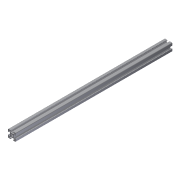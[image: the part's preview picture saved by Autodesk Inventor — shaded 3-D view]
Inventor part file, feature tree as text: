
AUTODESK INVENTOR PART (.ipt)
format: ipt  version: 2011 (Build 150239000, 239)  size: 166,912 bytes
history: native  units: in
note: dims shown in document units (in); Inventor stores cm internally (conversion verified against a paired STEP export)
features: extrude x1, sketch x1
ambient origin geometry x8: Origin, YZ Plane, XZ Plane, XY Plane, X Axis, Y Axis, Z Axis, Center Point
bodies: Solid1 (feature_tree)
feature tree (2):
  extrude  "Extrusion1"  [1 undecoded]
  sketch  "Sketch1"  dims[d0=15.9252in d1=0.0in]
note: 1 required parameter value undecoded (feature->parameter linkage not recoverable at this tier; creation-order binding heuristic only, values carry confidence <= 0.55)
